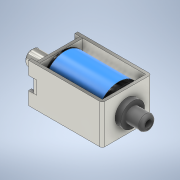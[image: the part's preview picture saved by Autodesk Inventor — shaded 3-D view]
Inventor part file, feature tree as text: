
AUTODESK INVENTOR PART (.ipt)
format: ipt  version: 2022 (Build 260153000, 153)  size: 332,800 bytes
history: native  units: mm
features: sketch x10, revolve x6, extrude x4, plane x2, fillet x1, chamfer x1, other x1, projected_geometry x1
ambient origin geometry x8: Origin, YZ Plane, XZ Plane, XY Plane, X Axis, Y Axis, Z Axis, Center Point
bodies: Solid1 (feature_tree), Solid2 (feature_tree), Solid3 (feature_tree), Solid4 (feature_tree), Solid5 (feature_tree), Solid6 (feature_tree), Solid7 (feature_tree), Solid8 (feature_tree)
feature tree (26):
  extrude  "Extrusion1"  Depth=10.0mm
  plane  "Work Plane1"
  sketch  "Sketch3"  dims[d4=0.6mm d5=8.0mm d6=0.0mm]
  plane  "Work Plane2"
  extrude  "Extrusion3"  Depth=0.5mm
  extrude  "Extrusion4"  Depth=8.0mm TaperAngle=0.0deg
  extrude  "Extrusion2"  Depth=20.75mm TaperAngle=0.0deg
  revolve  "Revolution1"  [1 undecoded]
  fillet  "Fillet1"  Radius=8.0mm
  revolve  "Revolution2"  [1 undecoded]
  chamfer  "Chamfer1"  Distance=3.0mm
  revolve  "Revolution3"  [1 undecoded]
  revolve  "Revolution4"  Angle=90.0deg
  sketch  "Sketch11"  dims[d57=0.6mm d58=3.0mm d59=0.75mm d60=90.0deg d61=0.4mm d62=2.0mm d63=45.0deg d64=90.0deg d65=90.0deg d66=90.0deg d67=90.0deg]
  revolve  "Revolution5"  Angle=45.0deg
  revolve  "Revolution6"  Angle=90.0deg
  sketch  "Sketch1"  dims[d0=15.0mm d1=10.0mm]
  sketch  "Sketch2"  dims[d2=0.5mm d3=0.5mm]
  other  "Image1"
  sketch  "Sketch4"  dims[d7=3.0mm d8=20.75mm d9=0.0mm]
  sketch  "Sketch5"  dims[d47=12.75mm d48=2.666667mm d49=8.0mm]
  projected_geometry  "Projected Loop1"
  sketch  "Sketch7"  dims[d50=0.6mm d51=0.0mm d52=12.35mm d53=0.0mm]
  sketch  "Sketch8"  dims[d54=3.0mm]
  sketch  "Sketch9"  dims[d55=0.75mm]
  sketch  "Sketch10"  dims[d56=360.0deg]
note: 3 required parameter values undecoded (feature->parameter linkage not recoverable at this tier; creation-order binding heuristic only, values carry confidence <= 0.55)
